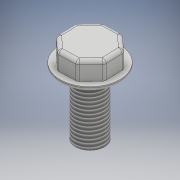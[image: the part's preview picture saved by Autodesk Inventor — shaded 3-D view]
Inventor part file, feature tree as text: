
AUTODESK INVENTOR PART (.ipt)
format: ipt  version: 2017 (Build 210142000, 142)  size: 163,840 bytes
history: native  units: mm
features: extrude x3, sketch x3, fillet x2, thread x1
ambient origin geometry x8: Origin, YZ Plane, XZ Plane, XY Plane, X Axis, Y Axis, Z Axis, Center Point
bodies: Solid1 (feature_tree)
feature tree (9):
  extrude  "Extrusion1"  Depth=2.0mm
  fillet  "Fillet1"  Radius=2.6mm
  extrude  "Extrusion2"  Depth=34.0mm
  fillet  "Fillet2"  Radius=34.0mm
  extrude  "Extrusion3"  [1 undecoded]
  thread  "Thread1"  [1 undecoded]
  sketch  "Sketch1"  dims[d0=10.0mm d1=0.0mm d2=2.0mm d3=2.6mm d4=0.0mm]
  sketch  "Sketch2"  dims[d5=2.0mm d7=16.0mm d8=34.0mm d9=0.0mm]
  sketch  "Sketch3"  dims[d10=10.0mm d11=0.0mm]
note: 2 required parameter values undecoded (feature->parameter linkage not recoverable at this tier; creation-order binding heuristic only, values carry confidence <= 0.55)
